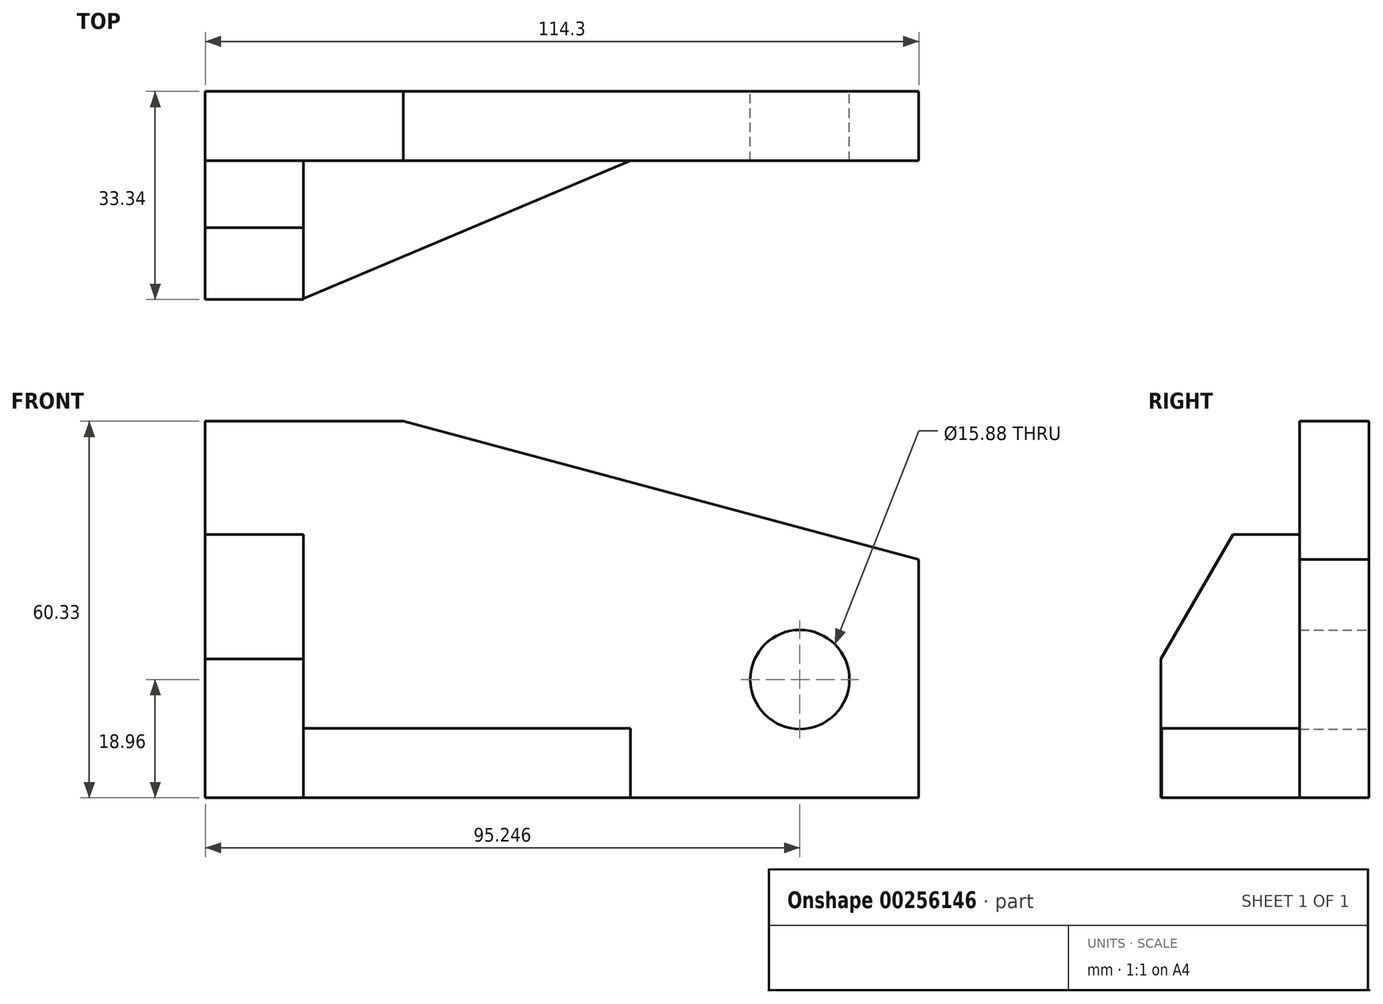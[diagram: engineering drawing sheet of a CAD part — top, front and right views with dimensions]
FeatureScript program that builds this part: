
annotation { "Feature Type Name" : "Feature", "Feature Type Description" : "" }
export const myFeature = defineFeature(function(context is Context, id is Id, definition is map)
    precondition{}
    {
        {
            var Q0;
            Q0=qCreatedBy(makeId("Front.planeOp"),FACE);
            var sketch = newSketch(context, id + "F0", { "sketchPlane" : qUnion([Q0])});
            skLineSegment(sketch, "E0.bottom", {"start": v(-63.43, 46.47) * mm, "end": v(-31.68, 46.47) * mm});
            skLineSegment(sketch, "E0.top", {"start": v(-63.43, -13.86) * mm, "end": v(50.87, -13.86) * mm});
            skLineSegment(sketch, "E0.left", {"start": v(-63.43, 46.47) * mm, "end": v(-63.43, -13.86) * mm});
            skLineSegment(sketch, "E0.right", {"start": v(50.87, 46.47) * mm, "end": v(50.87, -13.86) * mm});
            skLineSegment(sketch, "E1", {"start": v(-31.68, 46.47) * mm, "end": v(50.87, 24.35) * mm});
            skCircle(sketch, "E2", {"center": v(31.82, 5.1) * mm, "radius": 7.94 * mm});
            skLineSegment(sketch, "E3.bottom", {"start": v(-63.43, -13.86) * mm, "end": v(-63.43, -13.86) * mm});
            skLineSegment(sketch, "E3.top", {"start": v(-63.43, 8.28) * mm, "end": v(-63.43, 8.28) * mm});
            skLineSegment(sketch, "E4", {"start": v(-63.43, 28.34) * mm, "end": v(-47.72, 28.34) * mm});
            skLineSegment(sketch, "E5", {"start": v(-47.72, 28.34) * mm, "end": v(-47.72, -13.86) * mm});
            skSolve(sketch);
        }
        {
            var Q0;
            Q0 = qSketchRegion(id + "F0", true);
            extrude(context, id + "F1", {"entities" : qUnion([Q0]), "depth" : 11.1 * mm});
        }
        {
            var Q0;
            {var subQ4=sQuery(id+"F0.wireOp",EDGE,"E4");Q0=makeQuery(id+"F0.imprint","IMPRINT",FACE,{"disambiguationData":[TD([[makeQuery(id+"F0.imprint","IMPRINT",EDGE,{"derivedFrom":subQ4}),-1.0]])]});}
            extrude(context, id + "F2", {"entities" : qUnion([Q0]), "operationType" : NewBodyOperationType.ADD, "depth" : 33.34 * mm});
        }
        {
            var Q0;
            Q0=makeQuery(id+"F2.opExtrude","SWEPT_FACE",FACE,{"disambiguationData":[OSD([sQuery(id+"F0.wireOp",EDGE,"E5")])]});
            var sketch = newSketch(context, id + "F3", { "sketchPlane" : qUnion([Q0])});
            skLineSegment(sketch, "E6", {"start": v(-33.34, -13.86) * mm, "end": v(-33.34, 8.37) * mm});
            skLineSegment(sketch, "E7", {"start": v(-33.34, 8.37) * mm, "end": v(-21.8, 28.34) * mm});
            skLineSegment(sketch, "E8", {"start": v(-33.34, 8.37) * mm, "end": v(-33.34, 28.34) * mm});
            skLineSegment(sketch, "E9", {"start": v(-33.34, 28.34) * mm, "end": v(-21.8, 28.34) * mm});
            skSolve(sketch);
        }
        {
            var Q0;
            Q0=makeQuery(id+"F3.imprint","IMPRINT",FACE,{"disambiguationData":[TD([[makeQuery(id+"F3.imprint","IMPRINT",EDGE,{"derivedFrom":sQuery(id+"F3.wireOp",EDGE,"E7")}),1.0]])]});
            extrude(context, id + "F4", {"entities" : qUnion([Q0]), "operationType" : NewBodyOperationType.REMOVE, "oppositeDirection" : true, "depth" : 25.4 * mm});
        }
        {
            var Q0;
            Q0=makeQuery(id+"F1.opExtrude","CAP_FACE",FACE,{"disambiguationData":[OSD([sQuery(id+"F0.wireOp",EDGE,"E0.bottom"),sQuery(id+"F0.wireOp",EDGE,"E0.top"),sQuery(id+"F0.wireOp",EDGE,"E0.left"),sQuery(id+"F0.wireOp",EDGE,"E0.right"),sQuery(id+"F0.wireOp",EDGE,"E1"),sQuery(id+"F0.wireOp",EDGE,"E2")])],"isStart":false});
            var sketch = newSketch(context, id + "F5", { "sketchPlane" : qUnion([Q0])});
            skLineSegment(sketch, "E10", {"start": v(-47.72, -13.86) * mm, "end": v(4.66, -13.86) * mm});
            skLineSegment(sketch, "E11", {"start": v(4.66, -13.86) * mm, "end": v(4.66, -2.74) * mm});
            skLineSegment(sketch, "E12", {"start": v(4.66, -2.74) * mm, "end": v(-47.72, -2.74) * mm});
            skSolve(sketch);
        }
        {
            var Q0;
            {var subQ0=sQuery(id+"F5.wireOp",EDGE,"E10");Q0=makeQuery(id+"F5.imprint","IMPRINT",FACE,{"disambiguationData":[TD([[makeQuery(id+"F5.imprint","IMPRINT",EDGE,{"derivedFrom":subQ0}),1.0]])]});}
            extrude(context, id + "F6", {"entities" : qUnion([Q0]), "operationType" : NewBodyOperationType.ADD, "depth" : 22.1 * mm});
        }
        {
            var Q0;
            Q0=makeQuery(id+"F6.opExtrude","SWEPT_FACE",FACE,{"disambiguationData":[OSD([sQuery(id+"F5.wireOp",EDGE,"E12")])]});
            var sketch = newSketch(context, id + "F7", { "sketchPlane" : qUnion([Q0])});
            skLineSegment(sketch, "E13", {"start": v(-47.72, -11.11) * mm, "end": v(-47.72, -33.21) * mm});
            skLineSegment(sketch, "E14", {"start": v(-47.72, -33.21) * mm, "end": v(4.66, -33.21) * mm});
            skLineSegment(sketch, "E15", {"start": v(4.66, -33.21) * mm, "end": v(4.66, -11.11) * mm});
            skLineSegment(sketch, "E16", {"start": v(4.66, -11.11) * mm, "end": v(-47.72, -11.11) * mm});
            skLineSegment(sketch, "E17", {"start": v(-47.72, -33.21) * mm, "end": v(4.66, -11.11) * mm});
            skSolve(sketch);
        }
        {
            var Q0;
            Q0=makeQuery(id+"F7.imprint","IMPRINT",FACE,{"disambiguationData":[TD([[makeQuery(id+"F7.imprint","IMPRINT",EDGE,{"derivedFrom":sQuery(id+"F7.wireOp",EDGE,"E14")}),-1.0]])]});
            extrude(context, id + "F8", {"entities" : qUnion([Q0]), "operationType" : NewBodyOperationType.REMOVE, "oppositeDirection" : true, "depth" : 25.4 * mm});
        }
    });
